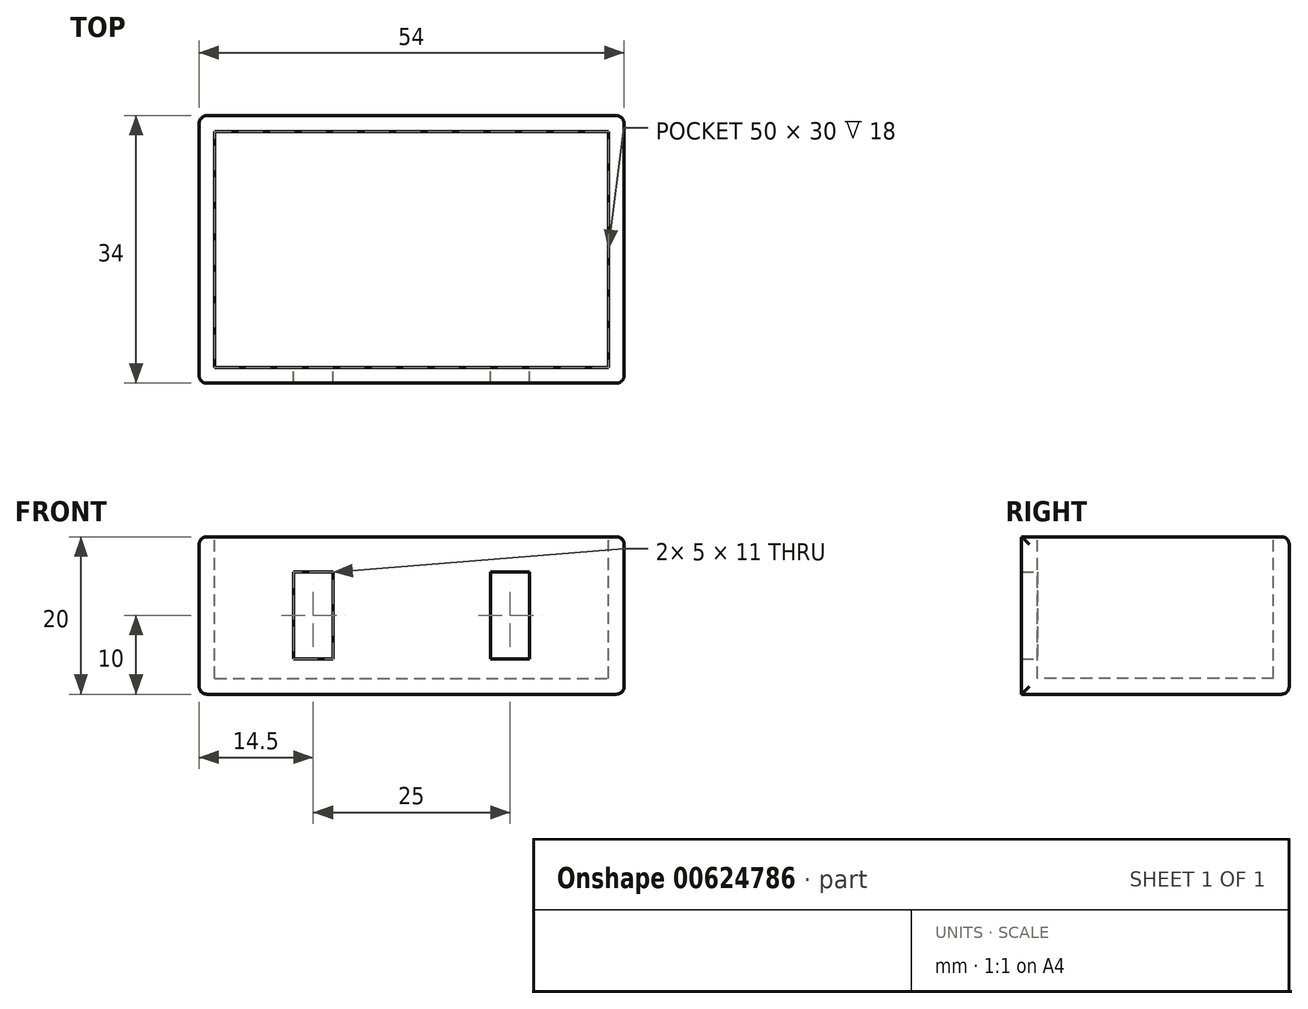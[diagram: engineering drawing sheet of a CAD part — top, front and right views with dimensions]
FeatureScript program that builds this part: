
annotation { "Feature Type Name" : "Feature", "Feature Type Description" : "" }
export const myFeature = defineFeature(function(context is Context, id is Id, definition is map)
    precondition{}
    {
        {
            var Q0;
            Q0=qCreatedBy(makeId("Front.planeOp"),FACE);
            var sketch = newSketch(context, id + "F0", { "sketchPlane" : qUnion([Q0])});
            skLineSegment(sketch, "E0.bottom", {"start": v(0, 0) * mm, "end": v(54, 0) * mm});
            skLineSegment(sketch, "E0.top", {"start": v(0, -20) * mm, "end": v(54, -20) * mm});
            skLineSegment(sketch, "E0.left", {"start": v(0, 0) * mm, "end": v(0, -20) * mm});
            skLineSegment(sketch, "E0.right", {"start": v(54, 0) * mm, "end": v(54, -20) * mm});
            skSolve(sketch);
        }
        {
            var Q0;
            Q0=qSketchRegion(id+"F0",true);
            extrude(context, id + "F1", {"entities" : qUnion([Q0]), "depth" : 34 * mm, "offsetDistance" : 25 * mm});
        }
        {
            var Q0;
            Q0=qCreatedBy(makeId("Top.planeOp"),FACE);
            var sketch = newSketch(context, id + "F2", { "sketchPlane" : qUnion([Q0])});
            skLineSegment(sketch, "E1.bottom", {"start": v(2, -2) * mm, "end": v(52, -2) * mm});
            skLineSegment(sketch, "E1.top", {"start": v(2, -32) * mm, "end": v(52, -32) * mm});
            skLineSegment(sketch, "E1.left", {"start": v(2, -2) * mm, "end": v(2, -32) * mm});
            skLineSegment(sketch, "E1.right", {"start": v(52, -2) * mm, "end": v(52, -32) * mm});
            skSolve(sketch);
        }
        {
            var Q0;
            Q0=qSketchRegion(id+"F2",true);
            extrude(context, id + "F3", {"entities" : qUnion([Q0]), "operationType" : NewBodyOperationType.REMOVE, "oppositeDirection" : true, "depth" : 18 * mm, "offsetDistance" : 25 * mm});
        }
        {
            var Q0;
            Q0=makeQuery(id+"F3.boolean.opBoolean","COPY",FACE,{"derivedFrom":makeQuery(id+"F3.opExtrude","SWEPT_FACE",FACE,{"disambiguationData":[OSD([sQuery(id+"F2.wireOp",EDGE,"E1.top")])]})});
            cPlane(context, id + "F4", {"entities" : qUnion([Q0]), "cplaneType" : CPlaneType.OFFSET, "offset" : 0 * mm, "width" : 150 * mm, "height" : 150 * mm});
        }
        {
            var Q0;
            Q0=qCreatedBy(id+"F4.planeOp",FACE);
            var sketch = newSketch(context, id + "F5", { "sketchPlane" : qUnion([Q0])});
            skLineSegment(sketch, "E2.bottom", {"start": v(-17, -4.5) * mm, "end": v(-12, -4.5) * mm});
            skLineSegment(sketch, "E3.top", {"start": v(-17, -15.5) * mm, "end": v(-12, -15.5) * mm});
            skLineSegment(sketch, "E4", {"start": v(-17, -4.5) * mm, "end": v(-17, -15.5) * mm});
            skLineSegment(sketch, "E5", {"start": v(-12, -4.5) * mm, "end": v(-12, -15.5) * mm});
            skLineSegment(sketch, "E6", {"start": v(-27, 0) * mm, "end": v(-27, -20) * mm, "construction": true});
            skLineSegment(sketch, "E7", {"start": v(0, -10) * mm, "end": v(-54, -10) * mm, "construction": true});
            skPoint(sketch, "E8", {"position": v(-27, -10) * mm});
            skPoint(sketch, "E9", {"position": v(-20.5, 2.87) * mm});
            skLineSegment(sketch, "E10.bottom", {"start": v(-42, -4.5) * mm, "end": v(-37, -4.5) * mm});
            skLineSegment(sketch, "E11.top", {"start": v(-42, -15.5) * mm, "end": v(-37, -15.5) * mm});
            skLineSegment(sketch, "E12", {"start": v(-42, -4.5) * mm, "end": v(-42, -15.5) * mm});
            skLineSegment(sketch, "E13", {"start": v(-37, -4.5) * mm, "end": v(-37, -15.5) * mm});
            skSolve(sketch);
        }
        {
            var Q0;
            Q0=qSketchRegion(id+"F5",true);
            extrude(context, id + "F6", {"entities" : qUnion([Q0]), "operationType" : NewBodyOperationType.REMOVE, "oppositeDirection" : true, "depth" : 5 * mm, "offsetDistance" : 25 * mm});
        }
        {
            var Q0;
            Q0=makeQuery(id+"F1.opExtrude","SWEPT_FACE",FACE,{"disambiguationData":[OSD([sQuery(id+"F0.wireOp",EDGE,"E0.right")])]});
            var Q1;
            Q1=makeQuery(id+"F1.opExtrude","CAP_FACE",FACE,{"disambiguationData":[OSD([sQuery(id+"F0.wireOp",EDGE,"E0.bottom"),sQuery(id+"F0.wireOp",EDGE,"E0.top"),sQuery(id+"F0.wireOp",EDGE,"E0.left"),sQuery(id+"F0.wireOp",EDGE,"E0.right")])],"isStart":true});
            var Q2;
            Q2=makeQuery(id+"F1.opExtrude","SWEPT_FACE",FACE,{"disambiguationData":[OSD([sQuery(id+"F0.wireOp",EDGE,"E0.left")])]});
            fillet(context, id + "F7", {"entities" : qUnion([Q0, Q1, Q2]), "radius" : 1 * mm, "tangentPropagation" : true, "allowEdgeOverflow" : false});
        }
    });
